# Revit family: Parametric door family
name_source: partatom
category: Doors
revit_build: Autodesk Revit 2016 (Build: 20150714_1515(x64)
units: mm (PartAtom-declared; Revit-internal decimal feet)

## family parameters
Always vertical = Yes
Cut with Voids When Loaded = No
Host = Wall
OmniClass Number = 23.30.10.00
OmniClass Title = Doors
Room Calculation Point = No
Shared = Yes

## types (1)
- Deur 1
    Breedte onderdorpel = 847 mm  [stored 2.77887 ft]
    Door paneel 1 = Deurpaneel 1
    Function = Interior
    Height = 2000 mm  [stored 6.56168 ft]
    Hoogte onderdorpel = 50 mm  [stored 0.164042 ft]
    Kopmaat = 47 mm  [stored 0.154199 ft]
    Kozijn_breedte = 67 mm
    Kozijn_diepte = 114 mm  [stored 0.374016 ft]
    Kozijn_sponning = 20 mm  [stored 0.0656168 ft]
    Onderdorpel = No
    Paneel_dikte = 25 mm  [stored 0.082021 ft]
    Rough Height = 2000 mm  [stored 6.56168 ft]
    Rough Width = 800 mm  [stored 2.62467 ft]
    Thickness = 25 mm  [stored 0.082021 ft]
    Wall Closure = By host
    Width = 800 mm  [stored 2.62467 ft]

note: [stored X ft] marks values corroborated as IEEE doubles in the binary element streams (Revit-internal decimal feet)

## geometry (parser evidence)
native form markers: Sweep x12
no freeform markers — native parametric forms only
